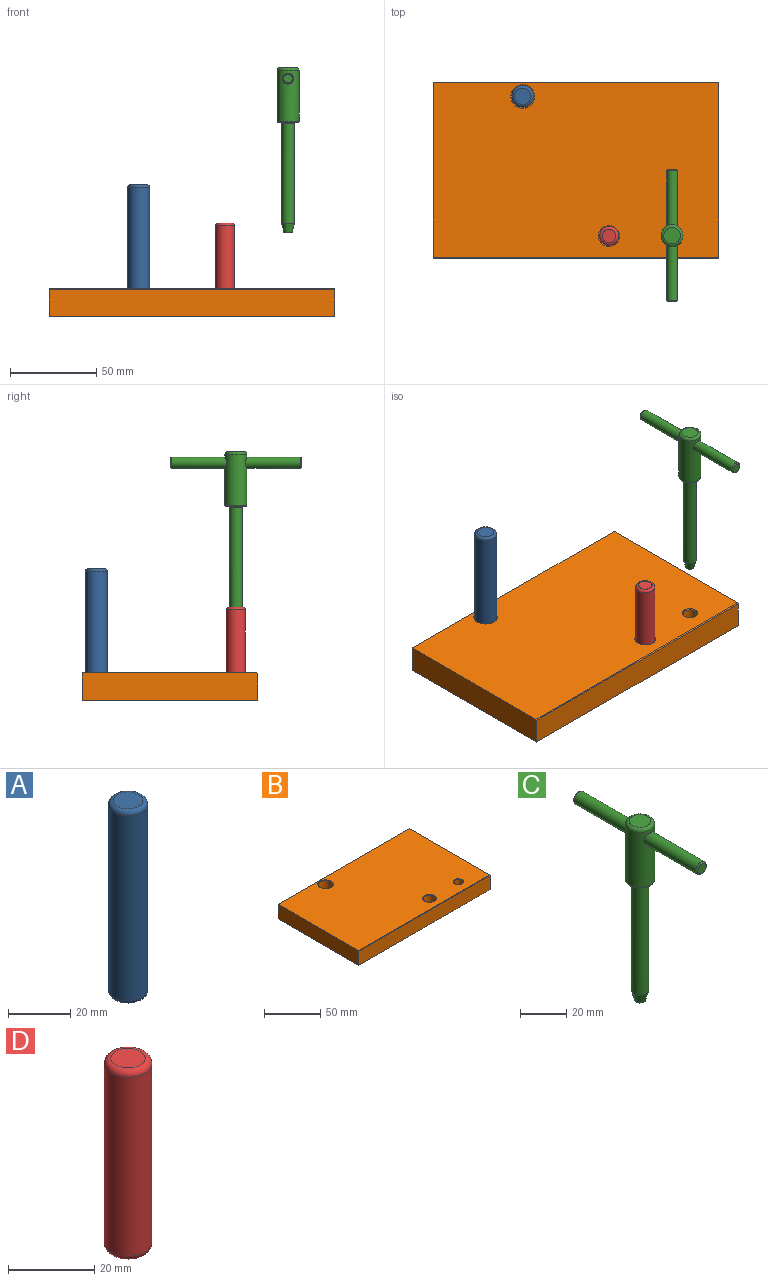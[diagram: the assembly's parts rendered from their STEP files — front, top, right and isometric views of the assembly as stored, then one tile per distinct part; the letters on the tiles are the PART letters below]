
ASSEMBLY  parts=4 mates=11
PART A: 5 faces, bbox 13.7x13.7x76.2 mm
  f0: cylinder r=6.35mm len=73.03mm, axis (0,0,-1), area 2913.6mm2, adj f3,f4
  f1: plane 9.53x9.53mm, normal (0,0,1), area 71.3mm2, adj f4
  f2: plane 9.53x9.53mm, normal (0,0,-1), area 71.3mm2, adj f3
  f3: torus R=4.76mm, axis (0,0,1), area 90.5mm2, adj f0,f2
  f4: torus R=4.76mm, axis (0,0,1), area 90.5mm2, adj f0,f1
PART B: 13 faces, bbox 165.1x101.6x15.9 mm
  f0: plane 165.1x15.37mm, normal (0,-1,0), area 2537.1mm2, adj f1,f5,f7,f12
  f1: plane 101.6x15.88mm, normal (1,0,0), area 1612.8mm2, adj f0,f2,f7,f8,f12
  f2: plane 165.1x15.88mm, normal (0,1,0), area 2621mm2, adj f1,f5,f7,f8
  f3: cylinder r=3.97mm len=15.37mm, axis (0,0,1), area 383.2mm2, adj f7,f9
  f4: cylinder r=5.56mm len=15.37mm, axis (0,0,1), area 536.5mm2, adj f7,f11
  f5: plane 101.6x15.88mm, normal (-1,0,0), area 1612.8mm2, adj f0,f2,f7,f8,f12
  f6: cylinder r=6.35mm len=15.37mm, axis (0,0,1), area 613.1mm2, adj f7,f10
  f7: plane 165.1x101.6mm, normal (0,0,-1), area 16501mm2, adj f0,f1,f2,f3,f4,f5,f6
  f8: plane 165.1x101.09mm, normal (0,0,1), area 16364mm2, adj f1,f2,f5,f9,f10,f11,f12
  f9: cone r=3.97mm half-angle=45deg, axis (0,0,1), area 19.1mm2, adj f3,f8
  f10: cone r=6.35mm half-angle=45deg, axis (0,0,1), area 29.8mm2, adj f6,f8
  f11: cone r=5.56mm half-angle=45deg, axis (0,0,1), area 26.2mm2, adj f4,f8
  f12: plane 165.1x0.51mm, normal (0,-0.71,0.71), area 118.6mm2, adj f0,f1,f5,f8
PART C: 15 faces, bbox 13.7x76.2x95.3 mm
  f0: cylinder r=6.35mm len=29.36mm, axis (0,0,-1), area 1105.9mm2, adj f4,f5,f7,f8
  f1: plane 9.55x9.55mm, normal (0,0,1), area 71.6mm2, adj f7
  f2: plane 11.07x11.07mm, normal (0,0,-1), area 43.1mm2, adj f8,f11
  f3: plane 5.08x5.08mm, normal (0,-1,0), area 20.3mm2, adj f14
  f4: cylinder r=3.17mm len=31.97mm, axis (0,-1,0), area 629.1mm2, adj f0,f14
  f5: cylinder r=3.17mm len=31.97mm, axis (0,-1,0), area 629mm2, adj f0,f13
  f6: plane 5.08x5.08mm, normal (0,1,0), area 20.3mm2, adj f13
  f7: torus R=4.78mm, axis (0,0,1), area 89.8mm2, adj f0,f1
  f8: torus R=5.54mm, axis (0,0,1), area 48.6mm2, adj f0,f2
  f9: cylinder r=3.73mm len=58.04mm, axis (0,0,1), area 1361.6mm2, adj f11,f12
  f10: plane 4.75x4.75mm, normal (0,0,-1), area 17.7mm2, adj f12
  f11: torus R=4.11mm, axis (0,0,1), area 14.6mm2, adj f2,f9
  f12: cone r=2.37mm half-angle=15deg, axis (0,0,1), area 100.9mm2, adj f9,f10
  f13: cone r=3.17mm half-angle=45deg, axis (0,-1,0), area 16.1mm2, adj f5,f6
  f14: cone r=2.54mm half-angle=45deg, axis (0,1,0), area 16.1mm2, adj f3,f4
PART D: 5 faces, bbox 12x12x54 mm
  f0: cylinder r=5.55mm len=50.83mm, axis (0,0,-1), area 1772.3mm2, adj f3,f4
  f1: plane 7.95x7.95mm, normal (0,0,1), area 49.6mm2, adj f4
  f2: plane 7.95x7.95mm, normal (0,0,-1), area 49.6mm2, adj f3
  f3: torus R=3.98mm, axis (0,0,1), area 77.4mm2, adj f0,f2
  f4: torus R=3.98mm, axis (0,0,1), area 77.4mm2, adj f0,f1
PLACE A t=(201.67,27.51,-28.63)mm
PLACE B t=(84.95,-8.76,-12.75)mm
PLACE C t=(140.53,-53.21,108.93)mm
PLACE D t=(232.72,26.12,-28.63)mm
MATE parallel A.f0 <-> B.f7  axis (0,0,-1) through (54.12,27.51,-28.63)mm
MATE parallel A.f0 <-> B.f6  axis (0,0,-1) through (54.12,27.51,-28.63)mm
MATE parallel A.f0 <-> B.f7  axis (0,0,-1) through (54.12,27.51,-28.63)mm
MATE cylindrical D.f0 <-> B.f4  axis (0,0,-1) through (104,-53.21,-27.05)mm
MATE cylindrical A.f0 <-> B.f6  axis (0,0,-1) through (54.12,27.51,-27.04)mm
MATE slider C.f9 <-> B.f3  axis (0,0,-1) through (140.53,-53.21,20.03)mm
MATE parallel B.f4 <-> B.f4  axis (0,0,-1) through (104,-53.21,-28.63)mm
MATE parallel B.f4 <-> B.f7  axis (0,0,-1) through (104,-53.21,-28.63)mm
MATE cylindrical B.f8 <-> B.f6  axis (0,0,1) through (84.88,-14.82,-12.75)mm
MATE parallel D.f0 <-> B.f7  axis (0,0,-1) through (104,-53.21,-28.63)mm
MATE parallel D.f0 <-> B.f4  axis (0,0,-1) through (104,-53.21,-28.63)mm
